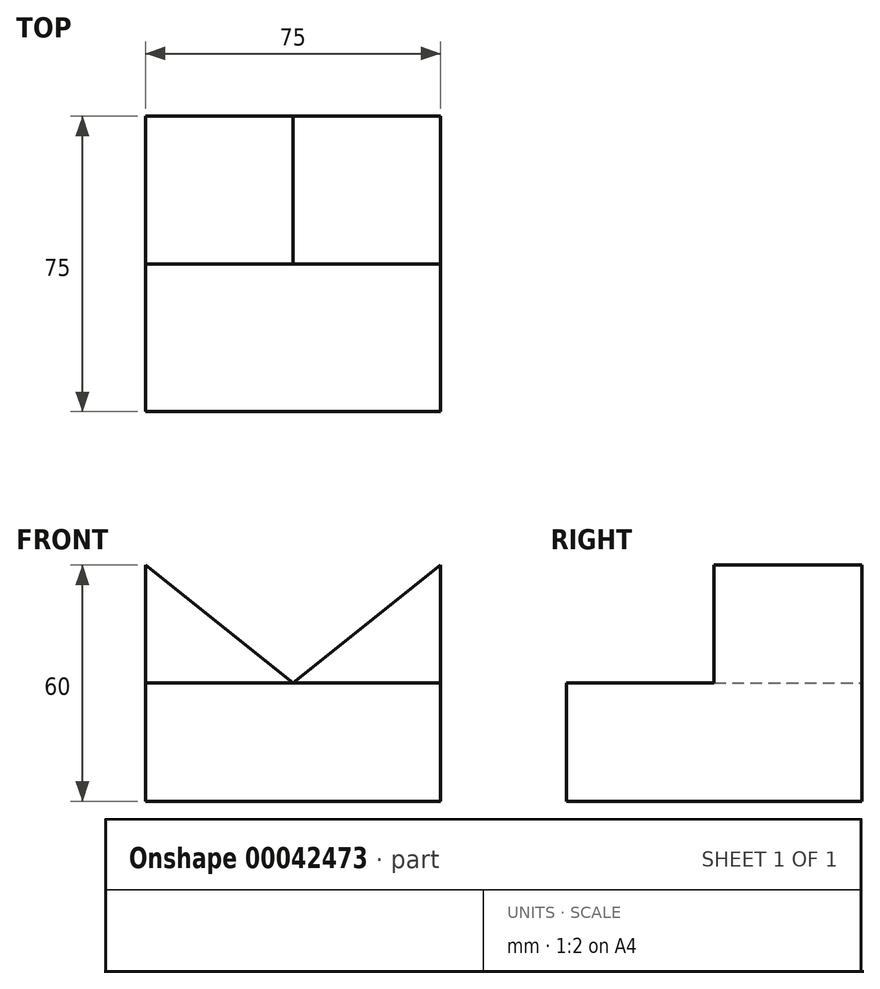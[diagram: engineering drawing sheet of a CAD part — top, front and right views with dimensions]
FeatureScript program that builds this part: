
annotation { "Feature Type Name" : "Feature", "Feature Type Description" : "" }
export const myFeature = defineFeature(function(context is Context, id is Id, definition is map)
    precondition{}
    {
        {
            var Q0;
            Q0=qCreatedBy(makeId("Front.planeOp"),FACE);
            var sketch = newSketch(context, id + "F0", { "sketchPlane" : qUnion([Q0])});
            skLineSegment(sketch, "E0.bottom", {"start": v(0, 0) * mm, "end": v(75, 0) * mm});
            skLineSegment(sketch, "E0.left", {"start": v(0, 0) * mm, "end": v(0, 60) * mm});
            skLineSegment(sketch, "E0.right", {"start": v(75, 0) * mm, "end": v(75, 60) * mm});
            skLineSegment(sketch, "E1", {"start": v(0, 30) * mm, "end": v(75, 30) * mm});
            skLineSegment(sketch, "E2", {"start": v(37.5, 30) * mm, "end": v(75, 60) * mm});
            skLineSegment(sketch, "E3", {"start": v(37.5, 30) * mm, "end": v(0, 60) * mm});
            skSolve(sketch);
        }
        {
            var Q0;
            {var subQ4=sQuery(id+"F0.wireOp",EDGE,"E0.bottom");Q0=makeQuery(id+"F0.imprint","IMPRINT",FACE,{"disambiguationData":[TD([[makeQuery(id+"F0.imprint","IMPRINT",EDGE,{"derivedFrom":subQ4}),1.0]])]});}
            extrude(context, id + "F1", {"entities" : qUnion([Q0]), "depth" : 75 * mm});
        }
        {
            var Q0;
            Q0 = qSketchRegion(id + "F0", true);
            extrude(context, id + "F2", {"entities" : qUnion([Q0]), "operationType" : NewBodyOperationType.ADD, "depth" : 37.5 * mm});
        }
    });
